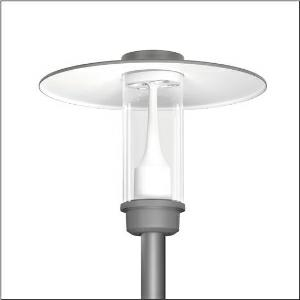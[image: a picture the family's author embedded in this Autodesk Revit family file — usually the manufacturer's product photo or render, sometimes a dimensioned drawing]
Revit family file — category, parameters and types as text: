
# Revit family: litepole_2_iq___p1_0a_5xa5425lf14h_94a7
name_source: partatom
category: Lighting Fixtures
units: mm (PartAtom-declared; Revit-internal decimal feet)

## family parameters
Cut with Voids When Loaded = No
Host = Face
Light Source = No
Part Type = Normal
Room Calculation Point = No
Round Connector Dimension = Use Diameter
Shared = No

## types (1)
- --- (1 x LED, 1520 lm, 10 W, 4000K)
    Apparent Load = 10 VA
    CIE Flux Codes = 33 62 89 96 100
    Color Rendering = 70
    Color Temperature = 4000K
    Default Elevation = 1800 mm
    Description = Litepole 2 iQ, mast luminaire, Module 540 iQ-SR, primary light control with 3 zone facetted reflector, of plastic, silver coated, highly specular, structured, primary optical cover: cover, of PMMA, transparent, light distribution: P1.0a, light emission: direct distribution, primary light characteristic: strongly asymmetric, installation type: post-top, LED, High Power LED, rated luminous flux: 1.520lm, luminous efficacy: 152lm/W, light colour: 740, colour temperature: 4000K, control gear: iQ Street-Remote, control: pre-setting: logarithmic dimming characteristic, Street-Remote, Auto-Match, Temp-Guard, Lumen-Switch, Night-Set, Smart-Wire, Light-Fading, Desk-Remote (wireless, voltage-free reading and setting of iQ features in the workshop via application-optimized NFC function/RFID function), optimised constant luminous flux control (CLO 2.0), with terminal, 6-pole, max. 2.5mm², mains connection: 230..240V, AC, 50/60Hz, start of lifetime: 10W, end of service life: 10W, reduction: 5W, luminaire housing, upper part, of aluminium, coated, Siteco® metallic grey (DB 702S), diameter: 750mm, height: 590mm, spigot size: d x l = 76 x 70mm (post-top) | with reducer (optional accessory) 60 x 70mm, mounting height: 3..5m, post-top mast mounting element, of diecast aluminium, coated, Siteco® metallic grey (DB 702S), Module 540 iQ-SR, traffic white (RAL 9016), equipment: standard, protection rating (complete): IP65, insulation class (complete): insulation class II (safety insulation), certification: CE, ENEC, VDE, packaging unit: 1 piece

Light Distribution: P1.0a
    Height = 590 mm
    Lamp = 1 x LED
    Lamp Light Flux = 1520 lm
    Lamp Power = 10 W
    Lamp count = 1
    Length = 750 mm
    Luminous efficacy = 152 lm/W
    Manufacturer = Siteco
    ModVariant = No
    Model = 5XA5425LF14H
    Number of Poles = 1
    OnlyDefault = Yes
    Power Factor = 1
    Product Name = Litepole 2 iQ | P1.0a
    Product group = mast luminaire | pylon top
    ProductGroupID = 6100
    Protection Class = Protection class II
    Protection Degree = IP 65
    RLX_Detail_Level = 1
    RLX_Emergency_Light_Flux = 0 lm
    RLX_Emergency_Type = 0
    RLX_Emergency_Type_DB = No
    RlxData = <blob elided: 59881 chars, md5=6c6a803b>
    Socket = socket
    Standby Power = 0 W
    System Light Flux = 1520 lm
    System Power = 10 W
    Type Comments = factory setting: luminous flux: 100 % | dim-lin: 254 | 401 mA
    Type Image = l_1006518.jpg
    URL = http://relux.com
    VarID = @adj_213781
    Voltage = 0 V
    Weight = 0.00 kg
    Width = 0 mm  [stored 0 ft]

note: [stored X ft] marks values corroborated as IEEE doubles in the binary element streams (Revit-internal decimal feet)

## geometry (parser evidence)
native form markers: Blend x4, Sweep x11
no freeform markers — native parametric forms only
